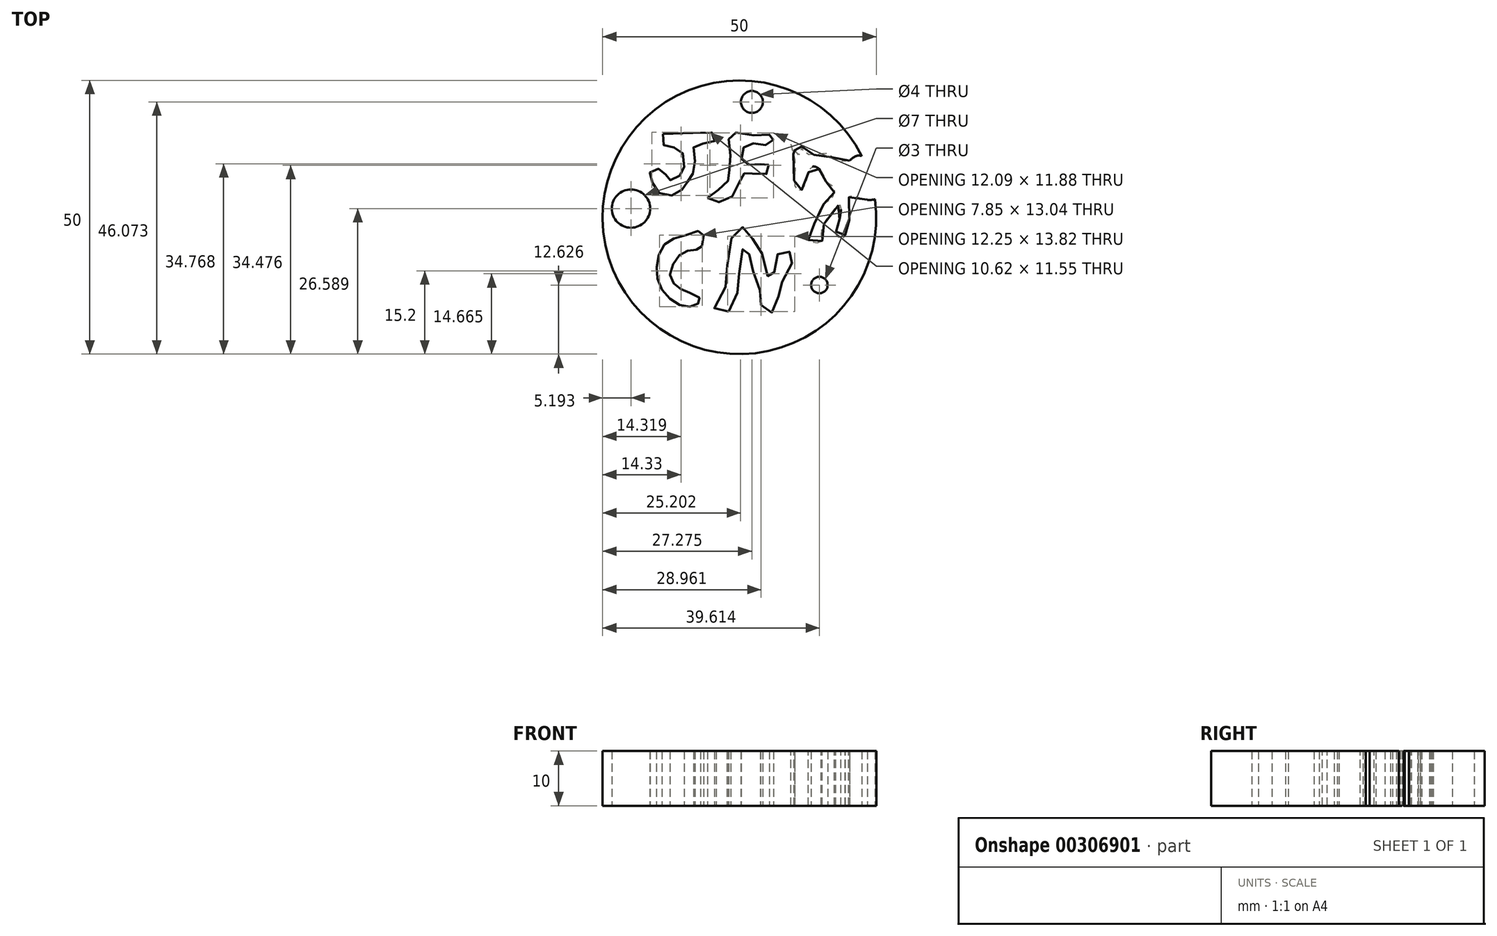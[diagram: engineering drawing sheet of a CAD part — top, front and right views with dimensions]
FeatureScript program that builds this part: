
annotation { "Feature Type Name" : "Feature", "Feature Type Description" : "" }
export const myFeature = defineFeature(function(context is Context, id is Id, definition is map)
    precondition{}
    {
        {
            var Q0;
            Q0=qCreatedBy(makeId("Top.planeOp"),FACE);
            var sketch = newSketch(context, id + "F0", { "sketchPlane" : qUnion([Q0])});
            skCircle(sketch, "E0", {"center": v(0, 0) * mm, "radius": 27.5 * mm});
            skCircle(sketch, "E1", {"center": v(0, 0) * mm, "radius": 25 * mm});
            skFitSpline(sketch, "E2", {"points": [v(-13.96, 15.23) * mm, v(-11.36, 15.23) * mm, v(-4.54, 15.23) * mm, v(-4.87, 13.6) * mm, v(-8.12, 13.28) * mm, v(-8.12, 10.36) * mm, v(-8.77, 7.43) * mm, v(-9.74, 6.14) * mm, v(-11.04, 4.51) * mm, v(-14.29, 4.19) * mm, v(-15.9, 6.46) * mm, v(-16.23, 8.4) * mm, v(-14.29, 8.73) * mm, v(-13.31, 7.43) * mm, v(-12.66, 6.79) * mm, v(-10.71, 7.76) * mm, v(-10.06, 9.7) * mm, v(-11.04, 12.63) * mm, v(-13.64, 12.95) * mm, v(-13.96, 15.23) * mm]});
            skFitSpline(sketch, "E3", {"points": [v(-5.84, 3.54) * mm, v(-2.6, 5.81) * mm, v(-1.95, 7.76) * mm, v(-1.62, 11.33) * mm, v(-1.62, 15.23) * mm, v(3.25, 14.9) * mm, v(6.17, 14.9) * mm, v(5.85, 13.6) * mm, v(3.9, 13.28) * mm, v(1.3, 13.28) * mm, v(0.33, 11) * mm, v(1.3, 9.7) * mm, v(3.9, 9.7) * mm, v(5.2, 9.7) * mm, v(5.2, 8.08) * mm, v(1.95, 8.08) * mm, v(0.98, 8.08) * mm, v(-0.32, 5.81) * mm, v(-2.6, 2.89) * mm, v(-5.84, 3.54) * mm]});
            skFitSpline(sketch, "E4", {"points": [v(-9.74, -3.28) * mm, v(-13.31, -4.58) * mm, v(-14.94, -7.83) * mm, v(-14.94, -11.4) * mm, v(-12.99, -14.65) * mm, v(-10.06, -16.27) * mm, v(-7.8, -15.95) * mm, v(-7.14, -14.97) * mm, v(-9.42, -13.67) * mm, v(-11.36, -12.7) * mm, v(-12.66, -10.75) * mm, v(-11.69, -7.83) * mm, v(-9.74, -6.2) * mm, v(-7.8, -5.88) * mm, v(-6.82, -5.23) * mm, v(-6.82, -2.63) * mm, v(-9.74, -3.28) * mm]});
            skFitSpline(sketch, "E5", {"points": [v(-1.95, -17.24) * mm, v(-0.32, -13.35) * mm, v(0, -9.45) * mm, v(0.98, -5.23) * mm, v(1.95, -7.5) * mm, v(2.6, -10.1) * mm, v(3.9, -14) * mm, v(3.9, -15.95) * mm, v(5.52, -17.57) * mm, v(6.82, -15.62) * mm, v(7.47, -13.02) * mm, v(8.44, -10.43) * mm, v(10.07, -6.85) * mm, v(8.44, -6.2) * mm, v(7.15, -6.53) * mm, v(6.5, -9.45) * mm, v(5.52, -11.4) * mm, v(4.55, -7.83) * mm, v(2.92, -4.58) * mm, v(1.3, -2.63) * mm, v(0, -1.66) * mm, v(-2.27, -7.18) * mm, v(-2.27, -12.05) * mm, v(-4.54, -16.92) * mm, v(-1.95, -17.24) * mm]});
            skFitSpline(sketch, "E6", {"points": [v(10.13, 10.26) * mm, v(10.07, 5.81) * mm, v(11.04, 4.84) * mm, v(12.34, 6.79) * mm, v(13, 9.06) * mm, v(14.29, 9.06) * mm, v(15.59, 7.1) * mm, v(15.91, 6.46) * mm, v(17.21, 5.49) * mm, v(16.89, 3.54) * mm, v(15.26, 2.24) * mm, v(13.64, -1.33) * mm, v(12.67, -3.93) * mm, v(12.67, -4.26) * mm, v(14.94, -4.58) * mm, v(14.94, -2.96) * mm, v(16.24, 0) * mm, v(18.37, 2.24) * mm, v(18.37, 0) * mm, v(18, -1.97) * mm, v(18, -1.97) * mm, v(17.62, -3.2) * mm, v(19.18, -3.61) * mm, v(19.3, -2.03) * mm, v(20.2, 0) * mm, v(20.13, 3.86) * mm, v(23.38, 3.21) * mm, v(24.5, 4.94) * mm, v(22.37, 11.16) * mm, v(20.13, 10.36) * mm, v(17.21, 10.68) * mm, v(15.91, 11.66) * mm, v(12.02, 11.66) * mm, v(11.37, 12.95) * mm, v(10.93, 11.4) * mm, v(9.42, 13.28) * mm, v(10.13, 10.26) * mm]});
            skCircle(sketch, "E7", {"center": v(2.27, 21.07) * mm, "radius": 2 * mm});
            skCircle(sketch, "E8", {"center": v(-19.8, 1.59) * mm, "radius": 3.5 * mm});
            skCircle(sketch, "E9", {"center": v(14.61, -12.37) * mm, "radius": 1.5 * mm});
            skFitSpline(sketch, "E10", {"points": [v(20.13, 10.36) * mm, v(22.37, 11.16) * mm, v(24.5, 4.94) * mm, v(23.38, 3.21) * mm, v(35.64, 5.97) * mm], "startDerivative": vector(12.97, 10.9) * mm, "endDerivative": vector(46.48, 12.26) * mm});
            skSolve(sketch);
        }
        {
            var Q0;
            Q0=makeQuery(id+"F0.imprint","IMPRINT",FACE,{"disambiguationData":[TD([[makeQuery(id+"F0.imprint","IMPRINT",EDGE,{"derivedFrom":sQuery(id+"F0.wireOp",EDGE,"E2")}),1.0]])]});
            extrude(context, id + "F1", {"entities" : qUnion([Q0]), "depth" : 10 * mm});
        }
    });
